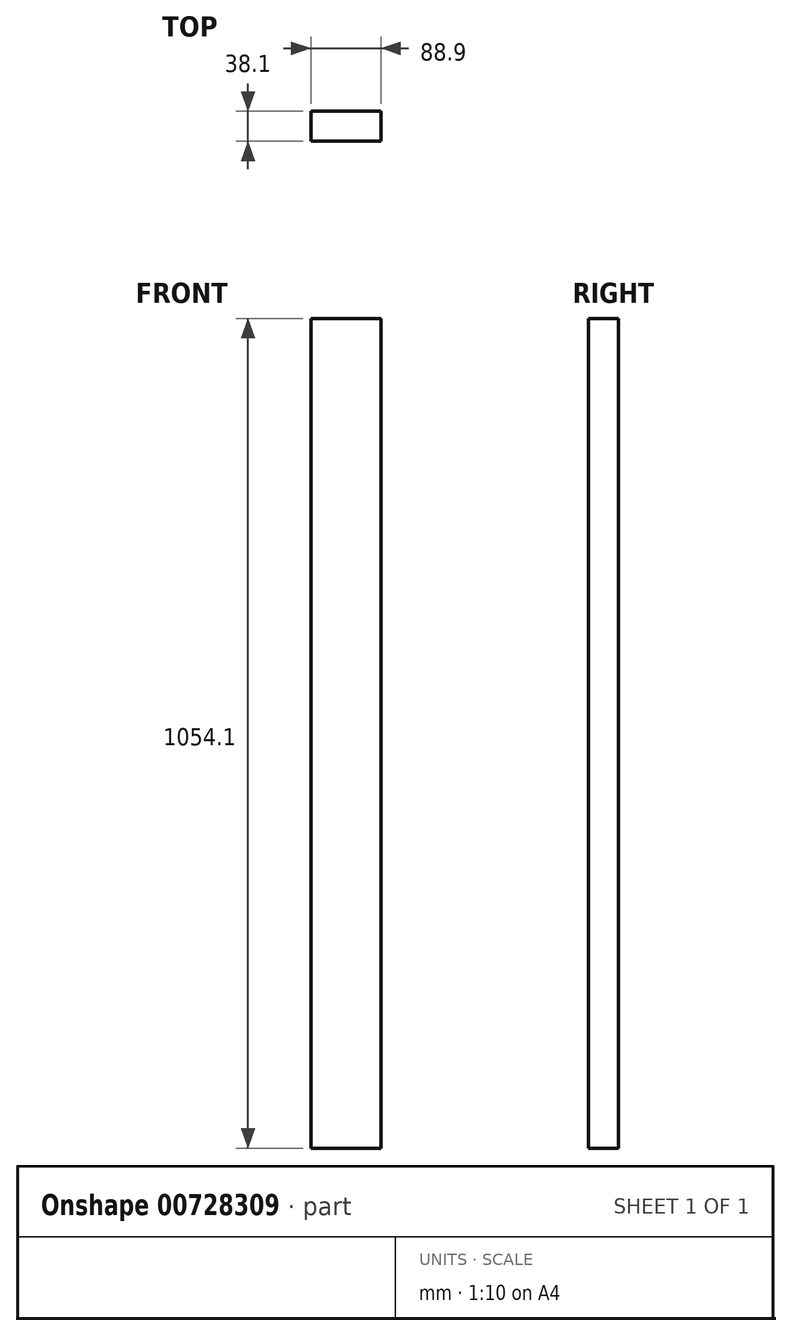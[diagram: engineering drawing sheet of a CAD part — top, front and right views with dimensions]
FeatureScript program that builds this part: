
annotation { "Feature Type Name" : "Feature", "Feature Type Description" : "" }
export const myFeature = defineFeature(function(context is Context, id is Id, definition is map)
    precondition{}
    {
        {
            var Q0;
            Q0=qCreatedBy(makeId("Front.planeOp"),FACE);
            var sketch = newSketch(context, id + "F0", { "sketchPlane" : qUnion([Q0])});
            skLineSegment(sketch, "E0.bottom", {"start": v(-44.45, -527.05) * mm, "end": v(44.45, -527.05) * mm});
            skLineSegment(sketch, "E0.top", {"start": v(-44.45, 527.05) * mm, "end": v(44.45, 527.05) * mm});
            skLineSegment(sketch, "E0.left", {"start": v(-44.45, -527.05) * mm, "end": v(-44.45, 527.05) * mm});
            skLineSegment(sketch, "E0.right", {"start": v(44.45, -527.05) * mm, "end": v(44.45, 527.05) * mm});
            skPoint(sketch, "E0.middle", {"position": v(0, 0) * mm});
            skSolve(sketch);
        }
        {
            var Q0;
            Q0=qSketchRegion(id+"F0",true);
            extrude(context, id + "F1", {"entities" : qUnion([Q0]), "depth" : 38.1 * mm});
        }
    });
